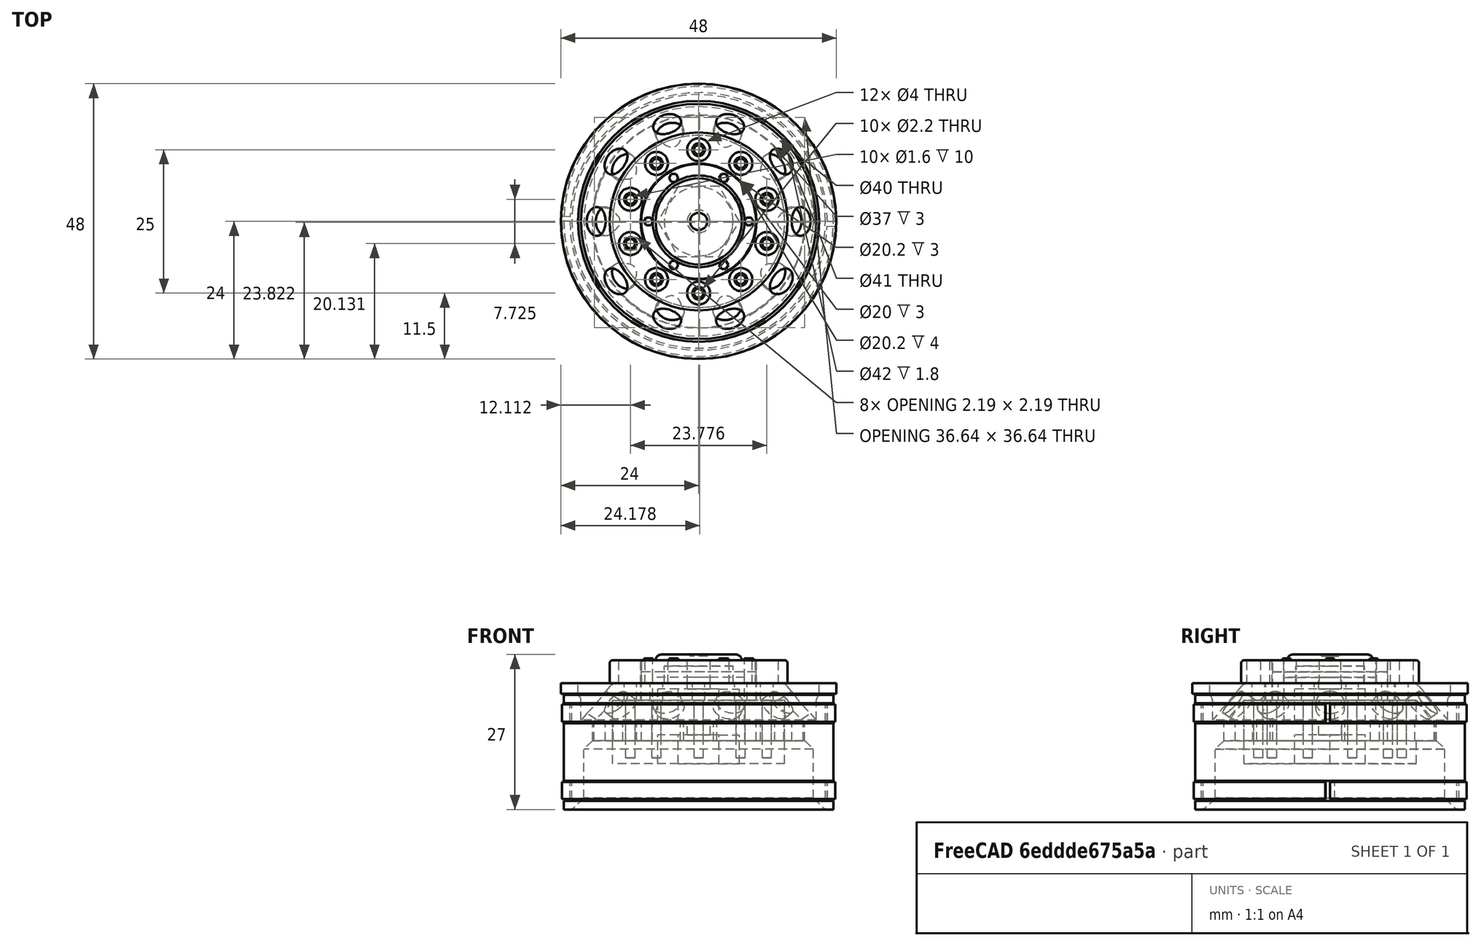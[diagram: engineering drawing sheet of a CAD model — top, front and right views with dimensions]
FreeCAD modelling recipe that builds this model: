
FCSTD DOCUMENT  (FreeCAD 0.18.4R)
Label: wheel_front_02
License: CC-BY 3.0
LicenseURL: http://creativecommons.org/licenses/by/3.0/
objects: Part::Cylinder×97, Part::MultiFuse×50, Part::Cut×30, Part::Feature×8, Part::Extrusion×8, Part::Fillet×7, Part::Mirroring×5, Part::Cone×2, Part::Chamfer×2
note: 209 computed .brp shape members not serialized (recipe doc carries the construction recipe); baked Part::Feature solids carry a one-line shape summary decoded from their .brp

FEATURE [Part::Cylinder] Cylinder
  Angle = 360
  AttacherType = Attacher::AttachEngine3D
  Height = 10
  Placement = pos=(0,0,0.5) rot=(0,0,1;0rad)
  Radius = 23.5
FEATURE [Part::Cylinder] Cylinder001
  Angle = 360
  AttacherType = Attacher::AttachEngine3D
  Height = 17
  Radius = 22
FEATURE [Part::Cut] Cut005
  Base = -> Cylinder
  Placement = pos=(0,0,4.5) rot=(0,0,1;0rad)
  Refine = true
  Tool = -> Cylinder001
FEATURE [Part::Cylinder] Cylinder002
  Angle = 360
  AttacherType = Attacher::AttachEngine3D
  Height = 20
  Radius = 23.5
FEATURE [Part::Cylinder] Cylinder003
  Angle = 360
  AttacherType = Attacher::AttachEngine3D
  Height = 17
  Radius = 23.5
FEATURE [Part::Cylinder] Cylinder004
  Angle = 360
  AttacherType = Attacher::AttachEngine3D
  Height = 17
  Radius = 22.1
FEATURE [Part::Cut] Cut007
  Base = -> Cylinder003
  Placement = pos=(0,0,1.5) rot=(0,0,1;0rad)
  Refine = true
  Tool = -> Cylinder004
FEATURE [Part::Cut] Cut006
  Base = -> Cylinder002
  Refine = true
  Tool = -> Cut007
FEATURE [Part::MultiFuse] Fusion001
  Refine = true
  Shapes = -> [Cut005,Cut006]
FEATURE [Part::Cylinder] Cylinder005
  Angle = 360
  AttacherType = Attacher::AttachEngine3D
  Height = 20
  Radius = 18.5
FEATURE [Part::Cut] Cut004
  Base = -> Fusion001
  Refine = true
  Tool = -> Cylinder005
FEATURE [Part::Cylinder] Cylinder006
  Angle = 360
  AttacherType = Attacher::AttachEngine3D
  Height = 10
  Placement = pos=(0,0,15) rot=(0,0,1;0rad)
  Radius = 20.5
FEATURE [Part::Cut] Cut003
  Base = -> Cut004
  Refine = true
  Tool = -> Cylinder006
FEATURE [Part::Fillet] Fillet002
  Base = -> Cut003
  Edges = 1 edges r=1: [Edge20]
FEATURE [Part::Cone] Cone
  Angle = 360
  AttacherType = Attacher::AttachEngine3D
  Height = 7
  Placement = pos=(0,0,15) rot=(0,0,1;0rad)
  Radius1 = 21
  Radius2 = 15
FEATURE [Part::Cylinder] Cylinder007
  Angle = 360
  AttacherType = Attacher::AttachEngine3D
  Height = 26
  Radius = 10
FEATURE [Part::Cut] Cut009
  Base = -> Cone
  Refine = true
  Tool = -> Cylinder007
FEATURE [Part::Cone] Cone001
  Angle = 360
  AttacherType = Attacher::AttachEngine3D
  Height = 10
  Placement = pos=(0,0,9) rot=(0,0,1;0rad)
  Radius1 = 24
  Radius2 = 15
FEATURE [Part::Cut] Cut008
  Base = -> Cut009
  Refine = true
  Tool = -> Cone001
FEATURE [Part::MultiFuse] Fusion
  Refine = true
  Shapes = -> [Fillet002,Cut008]
FEATURE [Part::Cylinder] Cylinder008
  Angle = 360
  AttacherType = Attacher::AttachEngine3D
  Height = 12
  Radius = 20
FEATURE [Part::Cut] Cut002
  Base = -> Fusion
  Refine = true
  Tool = -> Cylinder008
FEATURE [Part::Chamfer] Chamfer001
  Base = -> Cut002
  Edges = 1 edges r=1.49: [Edge39]
FEATURE [Part::Chamfer] Chamfer
  Base = -> Chamfer001
  Edges = 1 edges r=2: [Edge10]
FEATURE [Part::Cylinder] Cylinder009
  Angle = 360
  AttacherType = Attacher::AttachEngine3D
  Height = 8
  Placement = pos=(12,0,16) rot=(0,1,0;1.01229rad)
  Radius = 2.5
FEATURE [Part::Cylinder] Cylinder010
  Angle = 360
  AttacherType = Attacher::AttachEngine3D
  Height = 8
  Placement = pos=(12,0,16) rot=(0,1,0;1.01229rad)
  Radius = 2.5
FEATURE [Part::Mirroring] Part__Mirroring  label="Cylinder107 (Mirror #1)004"
  Base = (0,0,0)
  Normal = (1,0,0)
  Source = -> Cylinder010
FEATURE [Part::MultiFuse] Fusion003
  Refine = true
  Shapes = -> [Cylinder009,Part__Mirroring]
FEATURE [Part::Cylinder] Cylinder011
  Angle = 360
  AttacherType = Attacher::AttachEngine3D
  Height = 8
  Placement = pos=(12,0,16) rot=(0,1,0;1.01229rad)
  Radius = 2.5
FEATURE [Part::Cylinder] Cylinder012
  Angle = 360
  AttacherType = Attacher::AttachEngine3D
  Height = 8
  Placement = pos=(12,0,16) rot=(0,1,0;1.01229rad)
  Radius = 2.5
FEATURE [Part::Mirroring] Part__Mirroring001  label="Cylinder107 (Mirror #1)005"
  Base = (0,0,0)
  Normal = (1,0,0)
  Source = -> Cylinder012
FEATURE [Part::MultiFuse] Fusion004
  Placement = pos=(0,0,0) rot=(0,0,1;0.628319rad)
  Refine = true
  Shapes = -> [Cylinder011,Part__Mirroring001]
FEATURE [Part::Cylinder] Cylinder013
  Angle = 360
  AttacherType = Attacher::AttachEngine3D
  Height = 8
  Placement = pos=(12,0,16) rot=(0,1,0;1.01229rad)
  Radius = 2.5
FEATURE [Part::Cylinder] Cylinder014
  Angle = 360
  AttacherType = Attacher::AttachEngine3D
  Height = 8
  Placement = pos=(12,0,16) rot=(0,1,0;1.01229rad)
  Radius = 2.5
FEATURE [Part::Mirroring] Part__Mirroring002  label="Cylinder107 (Mirror #1)006"
  Base = (0,0,0)
  Normal = (1,0,0)
  Source = -> Cylinder014
FEATURE [Part::MultiFuse] Fusion005
  Placement = pos=(0,0,0) rot=(0,0,1;1.25664rad)
  Refine = true
  Shapes = -> [Cylinder013,Part__Mirroring002]
FEATURE [Part::Cylinder] Cylinder015
  Angle = 360
  AttacherType = Attacher::AttachEngine3D
  Height = 8
  Placement = pos=(12,0,16) rot=(0,1,0;1.01229rad)
  Radius = 2.5
FEATURE [Part::Cylinder] Cylinder016
  Angle = 360
  AttacherType = Attacher::AttachEngine3D
  Height = 8
  Placement = pos=(12,0,16) rot=(0,1,0;1.01229rad)
  Radius = 2.5
FEATURE [Part::Mirroring] Part__Mirroring003  label="Cylinder107 (Mirror #1)007"
  Base = (0,0,0)
  Normal = (1,0,0)
  Source = -> Cylinder016
FEATURE [Part::MultiFuse] Fusion006
  Placement = pos=(0,0,0) rot=(0,0,1;1.88496rad)
  Refine = true
  Shapes = -> [Cylinder015,Part__Mirroring003]
FEATURE [Part::Cylinder] Cylinder017
  Angle = 360
  AttacherType = Attacher::AttachEngine3D
  Height = 8
  Placement = pos=(12,0,16) rot=(0,1,0;1.01229rad)
  Radius = 2.5
FEATURE [Part::Cylinder] Cylinder018
  Angle = 360
  AttacherType = Attacher::AttachEngine3D
  Height = 8
  Placement = pos=(12,0,16) rot=(0,1,0;1.01229rad)
  Radius = 2.5
FEATURE [Part::Mirroring] Part__Mirroring004  label="Cylinder107 (Mirror #1)008"
  Base = (0,0,0)
  Normal = (1,0,0)
  Source = -> Cylinder018
FEATURE [Part::MultiFuse] Fusion007
  Placement = pos=(0,0,0) rot=(0,0,1;2.51327rad)
  Refine = true
  Shapes = -> [Cylinder017,Part__Mirroring004]
FEATURE [Part::MultiFuse] Fusion002
  Placement = pos=(0,0,-1) rot=(0,0,1;0rad)
  Refine = true
  Shapes = -> [Fusion003,Fusion004,Fusion005,Fusion006,Fusion007]
FEATURE [Part::Cut] Cut001
  Base = -> Chamfer
  Refine = true
  Tool = -> Fusion002
FEATURE [Part::Cylinder] Cylinder019
  Angle = 360
  AttacherType = Attacher::AttachEngine3D
  Height = 10
  Placement = pos=(12.5,0,13) rot=(0,0,1;0rad)
  Radius = 1.1
FEATURE [Part::Cylinder] Cylinder020
  Angle = 360
  AttacherType = Attacher::AttachEngine3D
  Height = 10
  Placement = pos=(-12.5,0,13) rot=(0,0,1;0rad)
  Radius = 1.1
FEATURE [Part::MultiFuse] Fusion009
  Placement = pos=(0,0,0) rot=(0,0,1;0.314159rad)
  Refine = true
  Shapes = -> [Cylinder019,Cylinder020]
FEATURE [Part::Cylinder] Cylinder021
  Angle = 360
  AttacherType = Attacher::AttachEngine3D
  Height = 10
  Placement = pos=(12.5,0,13) rot=(0,0,1;0rad)
  Radius = 1.1
FEATURE [Part::Cylinder] Cylinder022
  Angle = 360
  AttacherType = Attacher::AttachEngine3D
  Height = 10
  Placement = pos=(-12.5,0,13) rot=(0,0,1;0rad)
  Radius = 1.1
FEATURE [Part::MultiFuse] Fusion010
  Placement = pos=(0,0,0) rot=(0,0,1;0.942478rad)
  Refine = true
  Shapes = -> [Cylinder021,Cylinder022]
FEATURE [Part::Cylinder] Cylinder023
  Angle = 360
  AttacherType = Attacher::AttachEngine3D
  Height = 10
  Placement = pos=(12.5,0,13) rot=(0,0,1;0rad)
  Radius = 1.1
FEATURE [Part::Cylinder] Cylinder024
  Angle = 360
  AttacherType = Attacher::AttachEngine3D
  Height = 10
  Placement = pos=(-12.5,0,13) rot=(0,0,1;0rad)
  Radius = 1.1
FEATURE [Part::MultiFuse] Fusion011
  Placement = pos=(0,0,0) rot=(0,0,1;2.82743rad)
  Refine = true
  Shapes = -> [Cylinder023,Cylinder024]
FEATURE [Part::Cylinder] Cylinder025
  Angle = 360
  AttacherType = Attacher::AttachEngine3D
  Height = 10
  Placement = pos=(12.5,0,13) rot=(0,0,1;0rad)
  Radius = 1.1
FEATURE [Part::Cylinder] Cylinder026
  Angle = 360
  AttacherType = Attacher::AttachEngine3D
  Height = 10
  Placement = pos=(-12.5,0,13) rot=(0,0,1;0rad)
  Radius = 1.1
FEATURE [Part::MultiFuse] Fusion012
  Placement = pos=(0,0,0) rot=(0,0,1;2.19911rad)
  Refine = true
  Shapes = -> [Cylinder025,Cylinder026]
FEATURE [Part::Cylinder] Cylinder027
  Angle = 360
  AttacherType = Attacher::AttachEngine3D
  Height = 10
  Placement = pos=(12.5,0,13) rot=(0,0,1;0rad)
  Radius = 1.1
FEATURE [Part::Cylinder] Cylinder028
  Angle = 360
  AttacherType = Attacher::AttachEngine3D
  Height = 10
  Placement = pos=(-12.5,0,13) rot=(0,0,1;0rad)
  Radius = 1.1
FEATURE [Part::MultiFuse] Fusion013
  Placement = pos=(0,0,0) rot=(0,0,1;1.5708rad)
  Refine = true
  Shapes = -> [Cylinder027,Cylinder028]
FEATURE [Part::MultiFuse] Fusion008
  Refine = true
  Shapes = -> [Fusion009,Fusion010,Fusion011,Fusion012,Fusion013]
FEATURE [Part::Cut] Cut
  Base = -> Cut001
  Refine = true
  Tool = -> Fusion008
FEATURE [Part::Fillet] Fillet001
  Base = -> Cut
  Edges = 1 edges r=1.5: [Edge121]
FEATURE [Part::Fillet] Fillet  label="rim"
  Base = -> Fillet001
  Edges = 1 edges r=1.5: [Edge161]
FEATURE [Part::Cylinder] Cylinder029
  Angle = 360
  AttacherType = Attacher::AttachEngine3D
  Height = 4
  Placement = pos=(0,0,12) rot=(0,0,1;0rad)
  Radius = 15
FEATURE [Part::Cylinder] Cylinder030
  Angle = 360
  AttacherType = Attacher::AttachEngine3D
  Height = 3
  Placement = pos=(0,0,16) rot=(0,0,1;0rad)
  Radius = 15
FEATURE [Part::Cylinder] Cylinder031
  Angle = 360
  AttacherType = Attacher::AttachEngine3D
  Height = 7
  Placement = pos=(0,0,19) rot=(0,0,1;0rad)
  Radius = 10
FEATURE [Part::Cylinder] Cylinder032
  Angle = 360
  AttacherType = Attacher::AttachEngine3D
  Height = 4
  Placement = pos=(0,0,23) rot=(0,0,1;0rad)
  Radius = 8
FEATURE [Part::Cut] Cut013
  Base = -> Cylinder031
  Refine = true
  Tool = -> Cylinder032
FEATURE [Part::MultiFuse] Fusion016
  Refine = true
  Shapes = -> [Cylinder030,Cut013]
FEATURE [Part::MultiFuse] Fusion015
  Refine = true
  Shapes = -> [Cylinder029,Fusion016]
FEATURE [Part::Cylinder] Cylinder033
  Angle = 360
  AttacherType = Attacher::AttachEngine3D
  Height = 3
  Placement = pos=(0,0,12) rot=(0,0,1;0.139626rad)
  Radius = 18.4
FEATURE [Part::Cylinder] Cylinder034
  Angle = 360
  AttacherType = Attacher::AttachEngine3D
  Height = 3
  Placement = pos=(0,0,12) rot=(0,0,1;1.39626rad)
  Radius = 18.4
FEATURE [Part::Cylinder] Cylinder035
  Angle = 360
  AttacherType = Attacher::AttachEngine3D
  Height = 3
  Placement = pos=(0,0,12) rot=(0,0,1;2.6529rad)
  Radius = 18.4
FEATURE [Part::Cylinder] Cylinder036
  Angle = 360
  AttacherType = Attacher::AttachEngine3D
  Height = 3
  Placement = pos=(0,0,12) rot=(0,0,1;3.90954rad)
  Radius = 18.4
FEATURE [Part::Cylinder] Cylinder037
  Angle = 360
  AttacherType = Attacher::AttachEngine3D
  Height = 3
  Placement = pos=(0,0,12) rot=(0,0,-1;1.11701rad)
  Radius = 18.4
FEATURE [Part::MultiFuse] Fusion017
  Refine = true
  Shapes = -> [Cylinder033,Cylinder034,Cylinder035,Cylinder036,Cylinder037]
FEATURE [Part::MultiFuse] Fusion014
  Refine = true
  Shapes = -> [Fusion015,Fusion017]
FEATURE [Part::Cylinder] Cylinder038
  Angle = 360
  AttacherType = Attacher::AttachEngine3D
  Height = 17
  Placement = pos=(0,0,9) rot=(0,0,1;0rad)
  Radius = 2
FEATURE [Part::Cut] Cut012
  Base = -> Fusion014
  Refine = true
  Tool = -> Cylinder038
FEATURE [Part::Feature] Face
  shape: bbox 17.79 x 17.28 x 2e-07 mm, 1 faces, 0 solids (baked)
FEATURE [Part::Extrusion] Extrude
  Base = -> Face
  Dir = (0,0,6)
  DirMode = 0
  FaceMakerClass = Part::FaceMakerExtrusion
  LengthFwd = 0
  LengthRev = 0
  Placement = pos=(0,0,16) rot=(0,0,1;0rad)
  Solid = false
  Symmetric = false
FEATURE [Part::Cylinder] Cylinder039
  Angle = 360
  AttacherType = Attacher::AttachEngine3D
  Height = 4
  Placement = pos=(0,0,12) rot=(0,0,1;0rad)
  Radius = 10
FEATURE [Part::MultiFuse] Fusion018
  Placement = pos=(0,0,-1) rot=(0,0,1;0rad)
  Refine = true
  Shapes = -> [Extrude,Cylinder039]
FEATURE [Part::Cut] Cut011
  Base = -> Cut012
  Refine = true
  Tool = -> Fusion018
FEATURE [Part::Cylinder] Cylinder040
  Angle = 360
  AttacherType = Attacher::AttachEngine3D
  Height = 10
  Placement = pos=(12.5,0,13) rot=(0,0,1;0rad)
  Radius = 0.8
FEATURE [Part::Cylinder] Cylinder041
  Angle = 360
  AttacherType = Attacher::AttachEngine3D
  Height = 10
  Placement = pos=(-12.5,0,13) rot=(0,0,1;0rad)
  Radius = 0.8
FEATURE [Part::MultiFuse] Fusion020
  Placement = pos=(0,0,0) rot=(0,0,1;0.314159rad)
  Refine = true
  Shapes = -> [Cylinder040,Cylinder041]
FEATURE [Part::Cylinder] Cylinder042
  Angle = 360
  AttacherType = Attacher::AttachEngine3D
  Height = 10
  Placement = pos=(12.5,0,13) rot=(0,0,1;0rad)
  Radius = 0.8
FEATURE [Part::Cylinder] Cylinder043
  Angle = 360
  AttacherType = Attacher::AttachEngine3D
  Height = 10
  Placement = pos=(-12.5,0,13) rot=(0,0,1;0rad)
  Radius = 0.8
FEATURE [Part::MultiFuse] Fusion021
  Placement = pos=(0,0,0) rot=(0,0,1;0.942478rad)
  Refine = true
  Shapes = -> [Cylinder042,Cylinder043]
FEATURE [Part::Cylinder] Cylinder044
  Angle = 360
  AttacherType = Attacher::AttachEngine3D
  Height = 10
  Placement = pos=(12.5,0,13) rot=(0,0,1;0rad)
  Radius = 0.8
FEATURE [Part::Cylinder] Cylinder045
  Angle = 360
  AttacherType = Attacher::AttachEngine3D
  Height = 10
  Placement = pos=(-12.5,0,13) rot=(0,0,1;0rad)
  Radius = 0.8
FEATURE [Part::MultiFuse] Fusion022
  Placement = pos=(0,0,0) rot=(0,0,1;2.82743rad)
  Refine = true
  Shapes = -> [Cylinder044,Cylinder045]
FEATURE [Part::Cylinder] Cylinder046
  Angle = 360
  AttacherType = Attacher::AttachEngine3D
  Height = 10
  Placement = pos=(12.5,0,13) rot=(0,0,1;0rad)
  Radius = 0.8
FEATURE [Part::Cylinder] Cylinder047
  Angle = 360
  AttacherType = Attacher::AttachEngine3D
  Height = 10
  Placement = pos=(-12.5,0,13) rot=(0,0,1;0rad)
  Radius = 0.8
FEATURE [Part::MultiFuse] Fusion023
  Placement = pos=(0,0,0) rot=(0,0,1;2.19911rad)
  Refine = true
  Shapes = -> [Cylinder046,Cylinder047]
FEATURE [Part::Cylinder] Cylinder048
  Angle = 360
  AttacherType = Attacher::AttachEngine3D
  Height = 10
  Placement = pos=(12.5,0,13) rot=(0,0,1;0rad)
  Radius = 0.8
FEATURE [Part::Cylinder] Cylinder049
  Angle = 360
  AttacherType = Attacher::AttachEngine3D
  Height = 10
  Placement = pos=(-12.5,0,13) rot=(0,0,1;0rad)
  Radius = 0.8
FEATURE [Part::MultiFuse] Fusion024
  Placement = pos=(0,0,0) rot=(0,0,1;1.5708rad)
  Refine = true
  Shapes = -> [Cylinder048,Cylinder049]
FEATURE [Part::MultiFuse] Fusion019
  Placement = pos=(0,0,-2) rot=(0,0,1;0rad)
  Refine = true
  Shapes = -> [Fusion020,Fusion021,Fusion022,Fusion023,Fusion024]
FEATURE [Part::Cut] Cut010  label="hub-front"
  Base = -> Cut011
  Refine = true
  Tool = -> Fusion019
FEATURE [Part::Cylinder] Cylinder050
  Angle = 360
  AttacherType = Attacher::AttachEngine3D
  Height = 4
  Placement = pos=(0,0,22) rot=(0,0,1;0rad)
  Radius = 15.5
FEATURE [Part::Cylinder] Cylinder051
  Angle = 360
  AttacherType = Attacher::AttachEngine3D
  Height = 10
  Placement = pos=(12.5,0,13) rot=(0,0,1;0rad)
  Radius = 2
FEATURE [Part::Cylinder] Cylinder052
  Angle = 360
  AttacherType = Attacher::AttachEngine3D
  Height = 10
  Placement = pos=(-12.5,0,13) rot=(0,0,1;0rad)
  Radius = 2
FEATURE [Part::MultiFuse] Fusion026
  Placement = pos=(0,0,0) rot=(0,0,1;0.314159rad)
  Refine = true
  Shapes = -> [Cylinder051,Cylinder052]
FEATURE [Part::Cylinder] Cylinder053
  Angle = 360
  AttacherType = Attacher::AttachEngine3D
  Height = 10
  Placement = pos=(12.5,0,13) rot=(0,0,1;0rad)
  Radius = 2
FEATURE [Part::Cylinder] Cylinder054
  Angle = 360
  AttacherType = Attacher::AttachEngine3D
  Height = 10
  Placement = pos=(-12.5,0,13) rot=(0,0,1;0rad)
  Radius = 2
FEATURE [Part::MultiFuse] Fusion027
  Placement = pos=(0,0,0) rot=(0,0,1;0.942478rad)
  Refine = true
  Shapes = -> [Cylinder053,Cylinder054]
FEATURE [Part::Cylinder] Cylinder055
  Angle = 360
  AttacherType = Attacher::AttachEngine3D
  Height = 10
  Placement = pos=(12.5,0,13) rot=(0,0,1;0rad)
  Radius = 2
FEATURE [Part::Cylinder] Cylinder056
  Angle = 360
  AttacherType = Attacher::AttachEngine3D
  Height = 10
  Placement = pos=(-12.5,0,13) rot=(0,0,1;0rad)
  Radius = 2
FEATURE [Part::MultiFuse] Fusion028
  Placement = pos=(0,0,0) rot=(0,0,1;2.82743rad)
  Refine = true
  Shapes = -> [Cylinder055,Cylinder056]
FEATURE [Part::Cylinder] Cylinder057
  Angle = 360
  AttacherType = Attacher::AttachEngine3D
  Height = 10
  Placement = pos=(12.5,0,13) rot=(0,0,1;0rad)
  Radius = 2
FEATURE [Part::Cylinder] Cylinder058
  Angle = 360
  AttacherType = Attacher::AttachEngine3D
  Height = 10
  Placement = pos=(-12.5,0,13) rot=(0,0,1;0rad)
  Radius = 2
FEATURE [Part::MultiFuse] Fusion029
  Placement = pos=(0,0,0) rot=(0,0,1;2.19911rad)
  Refine = true
  Shapes = -> [Cylinder057,Cylinder058]
FEATURE [Part::Cylinder] Cylinder059
  Angle = 360
  AttacherType = Attacher::AttachEngine3D
  Height = 10
  Placement = pos=(12.5,0,13) rot=(0,0,1;0rad)
  Radius = 2
FEATURE [Part::Cylinder] Cylinder060
  Angle = 360
  AttacherType = Attacher::AttachEngine3D
  Height = 10
  Placement = pos=(-12.5,0,13) rot=(0,0,1;0rad)
  Radius = 2
FEATURE [Part::MultiFuse] Fusion030
  Placement = pos=(0,0,0) rot=(0,0,1;1.5708rad)
  Refine = true
  Shapes = -> [Cylinder059,Cylinder060]
FEATURE [Part::MultiFuse] Fusion025
  Placement = pos=(0,0,9) rot=(0,0,1;0rad)
  Refine = true
  Shapes = -> [Fusion026,Fusion027,Fusion028,Fusion029,Fusion030]
FEATURE [Part::Cut] Cut015
  Base = -> Cylinder050
  Refine = true
  Tool = -> Fusion025
FEATURE [Part::Fillet] Fillet004
  Base = -> Cut015
  Edges = 10 edges r=0.39: [Edge4,Edge5,Edge6,Edge7,Edge8,Edge9,Edge10,Edge11,Edge12,Edge13]
FEATURE [Part::Cylinder] Cylinder061
  Angle = 360
  AttacherType = Attacher::AttachEngine3D
  Height = 4
  Placement = pos=(0,0,22) rot=(0,0,1;0rad)
  Radius = 10.1
FEATURE [Part::Cut] Cut014
  Base = -> Fillet004
  Refine = true
  Tool = -> Cylinder061
FEATURE [Part::Fillet] Fillet003  label="hub-bolts-cover-front"
  Base = -> Cut014
  Edges = 1 edges r=0.49: [Edge1]
FEATURE [Part::Cylinder] Cylinder062
  Angle = 360
  AttacherType = Attacher::AttachEngine3D
  Height = 2
  Placement = pos=(0,0,-6) rot=(0,0,1;0rad)
  Radius = 7.5
FEATURE [Part::Fillet] Fillet006
  Base = -> Cylinder062
  Edges = 1 edges r=1: [Edge1]
  Placement = pos=(0,0,-6) rot=(0,0,1;0rad)
FEATURE [Part::Cylinder] Cylinder063
  Angle = 360
  AttacherType = Attacher::AttachEngine3D
  Height = 0.3
  Placement = pos=(0,0,-10.3) rot=(0,0,1;0rad)
  Radius = 1.5
FEATURE [Part::Cut] Cut016
  Base = -> Fillet006
  Refine = true
  Tool = -> Cylinder063
FEATURE [Part::Fillet] Fillet005
  Base = -> Cut016
  Edges = 1 edges r=0.29: [Edge6]
  Placement = pos=(0,0,48) rot=(0,0,1;0rad)
FEATURE [Part::Feature] Face001
  shape: bbox 1.791 x 1.578 x 2e-07 mm, 1 faces, 0 solids (baked)
FEATURE [Part::Extrusion] Extrude001
  Base = -> Face001
  Dir = (0,0,0.3)
  DirMode = 0
  FaceMakerClass = Part::FaceMakerExtrusion
  LengthFwd = 0
  LengthRev = 0
  Placement = pos=(-0.75,0,47.5) rot=(0,0,1;3.14159rad)
  Solid = false
  Symmetric = false
FEATURE [Part::Feature] Face002
  shape: bbox 1.791 x 1.578 x 2e-07 mm, 1 faces, 0 solids (baked)
FEATURE [Part::Extrusion] Extrude002
  Base = -> Face002
  Dir = (0,0,0.3)
  DirMode = 0
  FaceMakerClass = Part::FaceMakerExtrusion
  LengthFwd = 0
  LengthRev = 0
  Placement = pos=(0.75,0,47.5) rot=(0,0,1;0rad)
  Solid = false
  Symmetric = false
FEATURE [Part::MultiFuse] Fusion032
  Placement = pos=(0,0,0) rot=(0,0,1;4.18879rad)
  Refine = true
  Shapes = -> [Extrude001,Extrude002]
FEATURE [Part::Feature] Face003
  shape: bbox 1.791 x 1.578 x 2e-07 mm, 1 faces, 0 solids (baked)
FEATURE [Part::Extrusion] Extrude003
  Base = -> Face003
  Dir = (0,0,0.3)
  DirMode = 0
  FaceMakerClass = Part::FaceMakerExtrusion
  LengthFwd = 0
  LengthRev = 0
  Placement = pos=(-0.75,0,47.5) rot=(0,0,1;3.14159rad)
  Solid = false
  Symmetric = false
FEATURE [Part::Feature] Face004
  shape: bbox 1.791 x 1.578 x 2e-07 mm, 1 faces, 0 solids (baked)
FEATURE [Part::Extrusion] Extrude004
  Base = -> Face004
  Dir = (0,0,0.3)
  DirMode = 0
  FaceMakerClass = Part::FaceMakerExtrusion
  LengthFwd = 0
  LengthRev = 0
  Placement = pos=(0.75,0,47.5) rot=(0,0,1;0rad)
  Solid = false
  Symmetric = false
FEATURE [Part::MultiFuse] Fusion033
  Placement = pos=(0,0,0) rot=(0,0,1;2.0944rad)
  Refine = true
  Shapes = -> [Extrude003,Extrude004]
FEATURE [Part::Feature] Face005
  shape: bbox 1.791 x 1.578 x 2e-07 mm, 1 faces, 0 solids (baked)
FEATURE [Part::Extrusion] Extrude005
  Base = -> Face005
  Dir = (0,0,0.3)
  DirMode = 0
  FaceMakerClass = Part::FaceMakerExtrusion
  LengthFwd = 0
  LengthRev = 0
  Placement = pos=(-0.75,0,47.5) rot=(0,0,1;3.14159rad)
  Solid = false
  Symmetric = false
FEATURE [Part::Feature] Face006
  shape: bbox 1.791 x 1.578 x 2e-07 mm, 1 faces, 0 solids (baked)
FEATURE [Part::Extrusion] Extrude006
  Base = -> Face006
  Dir = (0,0,0.3)
  DirMode = 0
  FaceMakerClass = Part::FaceMakerExtrusion
  LengthFwd = 0
  LengthRev = 0
  Placement = pos=(0.75,0,47.5) rot=(0,0,1;0rad)
  Solid = false
  Symmetric = false
FEATURE [Part::MultiFuse] Fusion034
  Refine = true
  Shapes = -> [Extrude005,Extrude006]
FEATURE [Part::Cylinder] Cylinder064
  Angle = 360
  AttacherType = Attacher::AttachEngine3D
  Height = 2
  Placement = pos=(0,0,26) rot=(0,0,1;0rad)
  Radius = 10
FEATURE [Part::Cylinder] Cylinder065
  Angle = 360
  AttacherType = Attacher::AttachEngine3D
  Height = 2
  Placement = pos=(0,0,24) rot=(0,0,1;0rad)
  Radius = 8
FEATURE [Part::MultiFuse] Fusion035
  Refine = true
  Shapes = -> [Cylinder064,Cylinder065]
FEATURE [Part::Cylinder] Cylinder066
  Angle = 360
  AttacherType = Attacher::AttachEngine3D
  Height = 3.5
  Placement = pos=(0,0,24) rot=(0,0,1;0rad)
  Radius = 6
FEATURE [Part::Cut] Cut017
  Base = -> Fusion035
  Placement = pos=(0,0,9) rot=(0,0,1;0rad)
  Refine = true
  Tool = -> Cylinder066
FEATURE [Part::MultiFuse] Fusion031  label="hub-cap-front"
  Placement = pos=(0,0,-11) rot=(0,0,1;0rad)
  Refine = true
  Shapes = -> [Fillet005,Fusion032,Fusion033,Fusion034,Cut017]
FEATURE [Part::Cylinder] Cylinder067
  Angle = 178
  AttacherType = Attacher::AttachEngine3D
  Height = 3
  Placement = pos=(0,0,1.8) rot=(0,0,1;0rad)
  Radius = 23.8
FEATURE [Part::Cylinder] Cylinder068
  Angle = 360
  AttacherType = Attacher::AttachEngine3D
  Height = 17
  Radius = 22.45
FEATURE [Part::Cut] Cut018
  Base = -> Cylinder067
  Refine = true
  Tool = -> Cylinder068
FEATURE [Part::Cylinder] Cylinder069
  Angle = 178
  AttacherType = Attacher::AttachEngine3D
  Height = 3
  Placement = pos=(0,0,1.8) rot=(0,0,1;0rad)
  Radius = 23.8
FEATURE [Part::Cylinder] Cylinder070
  Angle = 360
  AttacherType = Attacher::AttachEngine3D
  Height = 17
  Radius = 22.45
FEATURE [Part::Cut] Cut019
  Base = -> Cylinder069
  Placement = pos=(0,0,0) rot=(0,0,1;3.14159rad)
  Refine = true
  Tool = -> Cylinder070
FEATURE [Part::MultiFuse] Fusion037
  Placement = pos=(0,0,13.5) rot=(0,0,1;0rad)
  Refine = true
  Shapes = -> [Cut018,Cut019]
FEATURE [Part::Cut] Cut020
  Base = -> Cylinder069
  Placement = pos=(0,0,0) rot=(0,0,1;3.14159rad)
  Refine = true
  Tool = -> Cylinder070
FEATURE [Part::Cut] Cut021
  Base = -> Cylinder067
  Refine = true
  Tool = -> Cylinder068
FEATURE [Part::MultiFuse] Fusion038
  Refine = true
  Shapes = -> [Cut021,Cut020]
FEATURE [Part::MultiFuse] Fusion036  label="rim-support-all"
  Refine = true
  Shapes = -> [Fusion037,Fusion038]
FEATURE [Part::Cylinder] Cylinder071
  Angle = 360
  AttacherType = Attacher::AttachEngine3D
  Height = 1.8
  Placement = pos=(0,0,20) rot=(0,0,1;0rad)
  Radius = 24
FEATURE [Part::Cylinder] Cylinder072
  Angle = 360
  AttacherType = Attacher::AttachEngine3D
  Height = 2
  Placement = pos=(0,0,20) rot=(0,0,1;0rad)
  Radius = 21
FEATURE [Part::Cut] Cut022  label="rim-support"
  Base = -> Cylinder071
  Placement = pos=(0,0,0.2) rot=(0,0,1;0rad)
  Refine = true
  Tool = -> Cylinder072
FEATURE [Part::Cylinder] Cylinder073
  Angle = 360
  AttacherType = Attacher::AttachEngine3D
  Height = 26
  Radius = 10.1
FEATURE [Part::Cut] Cut023  label="rim-front"
  Base = -> Fillet
  Refine = true
  Tool = -> Cylinder073
FEATURE [Part::Cylinder] Cylinder074
  Angle = 360
  AttacherType = Attacher::AttachEngine3D
  Height = 8
  Placement = pos=(0,0,8) rot=(0,0,1;0rad)
  Radius = 15
FEATURE [Part::Cylinder] Cylinder075
  Angle = 360
  AttacherType = Attacher::AttachEngine3D
  Height = 3
  Placement = pos=(0,0,16) rot=(0,0,1;0rad)
  Radius = 15
FEATURE [Part::Cylinder] Cylinder076
  Angle = 360
  AttacherType = Attacher::AttachEngine3D
  Height = 7
  Placement = pos=(0,0,19) rot=(0,0,1;0rad)
  Radius = 10
FEATURE [Part::Cylinder] Cylinder077
  Angle = 360
  AttacherType = Attacher::AttachEngine3D
  Height = 4
  Placement = pos=(0,0,23) rot=(0,0,1;0rad)
  Radius = 8
FEATURE [Part::Cut] Cut024
  Base = -> Cylinder076
  Refine = true
  Tool = -> Cylinder077
FEATURE [Part::MultiFuse] Fusion039
  Refine = true
  Shapes = -> [Cylinder075,Cut024]
FEATURE [Part::Cylinder] Cylinder078
  Angle = 360
  AttacherType = Attacher::AttachEngine3D
  Height = 3
  Placement = pos=(0,0,12) rot=(0,0,1;0.139626rad)
  Radius = 18.4
FEATURE [Part::Cylinder] Cylinder079
  Angle = 360
  AttacherType = Attacher::AttachEngine3D
  Height = 3
  Placement = pos=(0,0,12) rot=(0,0,1;1.39626rad)
  Radius = 18.4
FEATURE [Part::Cylinder] Cylinder080
  Angle = 360
  AttacherType = Attacher::AttachEngine3D
  Height = 3
  Placement = pos=(0,0,12) rot=(0,0,1;2.6529rad)
  Radius = 18.4
FEATURE [Part::Cylinder] Cylinder081
  Angle = 360
  AttacherType = Attacher::AttachEngine3D
  Height = 3
  Placement = pos=(0,0,12) rot=(0,0,1;3.90954rad)
  Radius = 18.4
FEATURE [Part::Cylinder] Cylinder082
  Angle = 360
  AttacherType = Attacher::AttachEngine3D
  Height = 3
  Placement = pos=(0,0,12) rot=(0,0,-1;1.11701rad)
  Radius = 18.4
FEATURE [Part::MultiFuse] Fusion040
  Refine = true
  Shapes = -> [Cylinder078,Cylinder079,Cylinder080,Cylinder081,Cylinder082]
FEATURE [Part::Cylinder] Cylinder083
  Angle = 360
  AttacherType = Attacher::AttachEngine3D
  Height = 17
  Placement = pos=(0,0,9) rot=(0,0,1;0rad)
  Radius = 2
FEATURE [Part::Feature] Face007
  shape: bbox 17.79 x 17.28 x 2e-07 mm, 1 faces, 0 solids (baked)
FEATURE [Part::Extrusion] Extrude007
  Base = -> Face007
  Dir = (0,0,6)
  DirMode = 0
  FaceMakerClass = Part::FaceMakerExtrusion
  LengthFwd = 0
  LengthRev = 0
  Placement = pos=(0,0,16) rot=(0,0,1;0rad)
  Solid = false
  Symmetric = false
FEATURE [Part::Cylinder] Cylinder084
  Angle = 360
  AttacherType = Attacher::AttachEngine3D
  Height = 4
  Placement = pos=(0,0,12) rot=(0,0,1;0rad)
  Radius = 10
FEATURE [Part::MultiFuse] Fusion041
  Placement = pos=(0,0,-9) rot=(0,0,1;0rad)
  Refine = true
  Shapes = -> [Extrude007,Cylinder084]
FEATURE [Part::Cylinder] Cylinder085
  Angle = 360
  AttacherType = Attacher::AttachEngine3D
  Height = 10
  Placement = pos=(12.5,0,13) rot=(0,0,1;0rad)
  Radius = 0.8
FEATURE [Part::Cylinder] Cylinder086
  Angle = 360
  AttacherType = Attacher::AttachEngine3D
  Height = 10
  Placement = pos=(-12.5,0,13) rot=(0,0,1;0rad)
  Radius = 0.8
FEATURE [Part::MultiFuse] Fusion043
  Placement = pos=(0,0,0) rot=(0,0,1;0.314159rad)
  Refine = true
  Shapes = -> [Cylinder085,Cylinder086]
FEATURE [Part::Cylinder] Cylinder087
  Angle = 360
  AttacherType = Attacher::AttachEngine3D
  Height = 10
  Placement = pos=(12.5,0,13) rot=(0,0,1;0rad)
  Radius = 0.8
FEATURE [Part::Cylinder] Cylinder088
  Angle = 360
  AttacherType = Attacher::AttachEngine3D
  Height = 10
  Placement = pos=(-12.5,0,13) rot=(0,0,1;0rad)
  Radius = 0.8
FEATURE [Part::MultiFuse] Fusion044
  Placement = pos=(0,0,0) rot=(0,0,1;0.942478rad)
  Refine = true
  Shapes = -> [Cylinder087,Cylinder088]
FEATURE [Part::Cylinder] Cylinder089
  Angle = 360
  AttacherType = Attacher::AttachEngine3D
  Height = 10
  Placement = pos=(12.5,0,13) rot=(0,0,1;0rad)
  Radius = 0.8
FEATURE [Part::Cylinder] Cylinder090
  Angle = 360
  AttacherType = Attacher::AttachEngine3D
  Height = 10
  Placement = pos=(-12.5,0,13) rot=(0,0,1;0rad)
  Radius = 0.8
FEATURE [Part::MultiFuse] Fusion045
  Placement = pos=(0,0,0) rot=(0,0,1;2.82743rad)
  Refine = true
  Shapes = -> [Cylinder089,Cylinder090]
FEATURE [Part::Cylinder] Cylinder091
  Angle = 360
  AttacherType = Attacher::AttachEngine3D
  Height = 10
  Placement = pos=(12.5,0,13) rot=(0,0,1;0rad)
  Radius = 0.8
FEATURE [Part::Cylinder] Cylinder092
  Angle = 360
  AttacherType = Attacher::AttachEngine3D
  Height = 10
  Placement = pos=(-12.5,0,13) rot=(0,0,1;0rad)
  Radius = 0.8
FEATURE [Part::MultiFuse] Fusion046
  Placement = pos=(0,0,0) rot=(0,0,1;2.19911rad)
  Refine = true
  Shapes = -> [Cylinder091,Cylinder092]
FEATURE [Part::Cylinder] Cylinder093
  Angle = 360
  AttacherType = Attacher::AttachEngine3D
  Height = 10
  Placement = pos=(12.5,0,13) rot=(0,0,1;0rad)
  Radius = 0.8
FEATURE [Part::Cylinder] Cylinder094
  Angle = 360
  AttacherType = Attacher::AttachEngine3D
  Height = 10
  Placement = pos=(-12.5,0,13) rot=(0,0,1;0rad)
  Radius = 0.8
FEATURE [Part::MultiFuse] Fusion047
  Placement = pos=(0,0,0) rot=(0,0,1;1.5708rad)
  Refine = true
  Shapes = -> [Cylinder093,Cylinder094]
FEATURE [Part::MultiFuse] Fusion042
  Placement = pos=(0,0,-4) rot=(0,0,1;0rad)
  Refine = true
  Shapes = -> [Fusion043,Fusion044,Fusion045,Fusion046,Fusion047]
FEATURE [Part::Cylinder] Cylinder095
  Angle = 360
  AttacherType = Attacher::AttachEngine3D
  Height = 17
  Placement = pos=(0,0,15) rot=(0,0,1;0rad)
  Radius = 8
FEATURE [Part::Cylinder] Cylinder096
  Angle = 360
  AttacherType = Attacher::AttachEngine3D
  Height = 2
  Placement = pos=(0,0,24) rot=(0,0,1;0rad)
  Radius = 10
FEATURE [Part::MultiFuse] Fusion048
  Refine = true
  Shapes = -> [Cylinder074,Fusion039]
FEATURE [Part::MultiFuse] Fusion049
  Refine = true
  Shapes = -> [Fusion048,Fusion040]
FEATURE [Part::Cut] Cut025
  Base = -> Fusion049
  Refine = true
  Tool = -> Cylinder083
FEATURE [Part::Cut] Cut026
  Base = -> Cut025
  Refine = true
  Tool = -> Fusion041
FEATURE [Part::Cut] Cut027
  Base = -> Cut026
  Refine = true
  Tool = -> Cylinder095
FEATURE [Part::Cut] Cut028
  Base = -> Cut027
  Refine = true
  Tool = -> Cylinder096
FEATURE [Part::Cut] Cut029  label="hub-front-metal-axle"
  Base = -> Cut028
  Refine = true
  Tool = -> Fusion042
